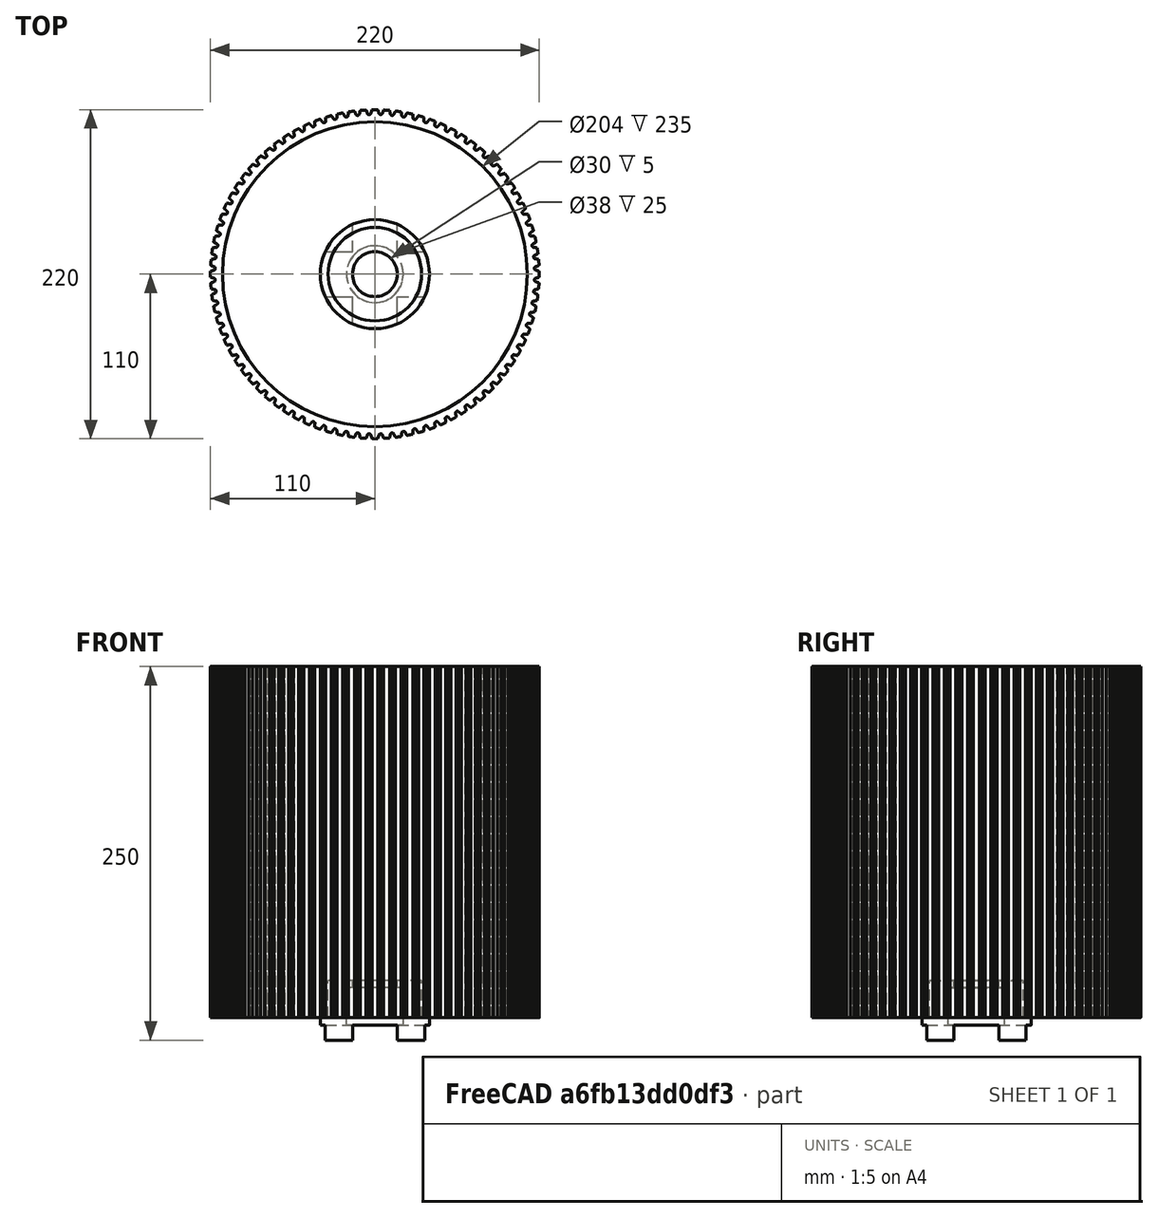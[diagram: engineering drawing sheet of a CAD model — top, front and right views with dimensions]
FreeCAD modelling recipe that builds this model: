
FCSTD DOCUMENT  (FreeCAD 0.15R4671 (Git))
Label: pica-large
License: All rights reserved
LicenseURL: http://en.wikipedia.org/wiki/All_rights_reserved
objects: Part::Cylinder×7, Part::Cut×5, Part::MultiFuse×3, Part::Box×2, Part::Part2DObjectPython×1, PartDesign::Pad×1
note: 20 computed .brp shape members not serialized (recipe doc carries the construction recipe); baked Part::Feature solids carry a one-line shape summary decoded from their .brp

FEATURE [Part::Part2DObjectPython] InvoluteGear  # Draft 2D object (typed FeaturePython)
  ExternalGear = true
  HighPrecision = true
  Modules = 2.5
  NumberOfTeeth = 88
  PressureAngle = 20
FEATURE [PartDesign::Pad] Pad
  Length = 235
  Length2 = 100
  Sketch = -> InvoluteGear
  Type = 0
FEATURE [Part::Cylinder] Cylinder
  Angle = 360
  Height = 300
  Placement = pos=(0,0,-10) rot=(0,0,1;0rad)
  Radius = 102
FEATURE [Part::Cut] Cut  label="Final"
  Base = -> Pad
  Tool = -> Cylinder
FEATURE [Part::Cylinder] Cylinder001
  Angle = 360
  Height = 400
  Radius = 110
FEATURE [Part::Cylinder] Cylinder002
  Angle = 360
  Height = 400
  Radius = 120
FEATURE [Part::Cut] Cut001
  Base = -> Cylinder002
  Tool = -> Cylinder001
FEATURE [Part::Cut] Cut002  label="Shade"
  Base = -> Cut
  Placement = pos=(0,0,15) rot=(0,0,1;0rad)
  Tool = -> Cut001
FEATURE [Part::Cylinder] Cylinder003
  Angle = 360
  Height = 15
  Radius = 36.5
FEATURE [Part::Cylinder] Cylinder004
  Angle = 360
  Height = 40
  Radius = 31.3
FEATURE [Part::MultiFuse] Fusion  label="Base Fusion"
  Shapes = -> [Cylinder004,Cylinder003]
FEATURE [Part::Box] Box  label="Cube"
  Height = 10
  Length = 100
  Placement = pos=(-50,-15,0) rot=(0,0,1;0rad)
  Width = 30
FEATURE [Part::Box] Box001  label="Cube001"
  Height = 10
  Length = 100
  Placement = pos=(15,-50,0) rot=(0,0,1;1.5708rad)
  Width = 30
FEATURE [Part::MultiFuse] Fusion001  label="Feet Cutout Fusion"
  Shapes = -> [Box001,Box]
FEATURE [Part::Cut] Cut003  label="Plain Base"
  Base = -> Fusion
  Tool = -> Fusion001
FEATURE [Part::Cylinder] Cylinder005
  Angle = 360
  Height = 50
  Radius = 15
FEATURE [Part::Cylinder] Cylinder006
  Angle = 360
  Height = 35
  Radius = 19
FEATURE [Part::MultiFuse] Fusion002  label="Fixture Mount"
  Shapes = -> [Cylinder005,Cylinder006]
FEATURE [Part::Cut] Cut004  label="Base w/ Mount"
  Base = -> Cut003
  Tool = -> Fusion002
